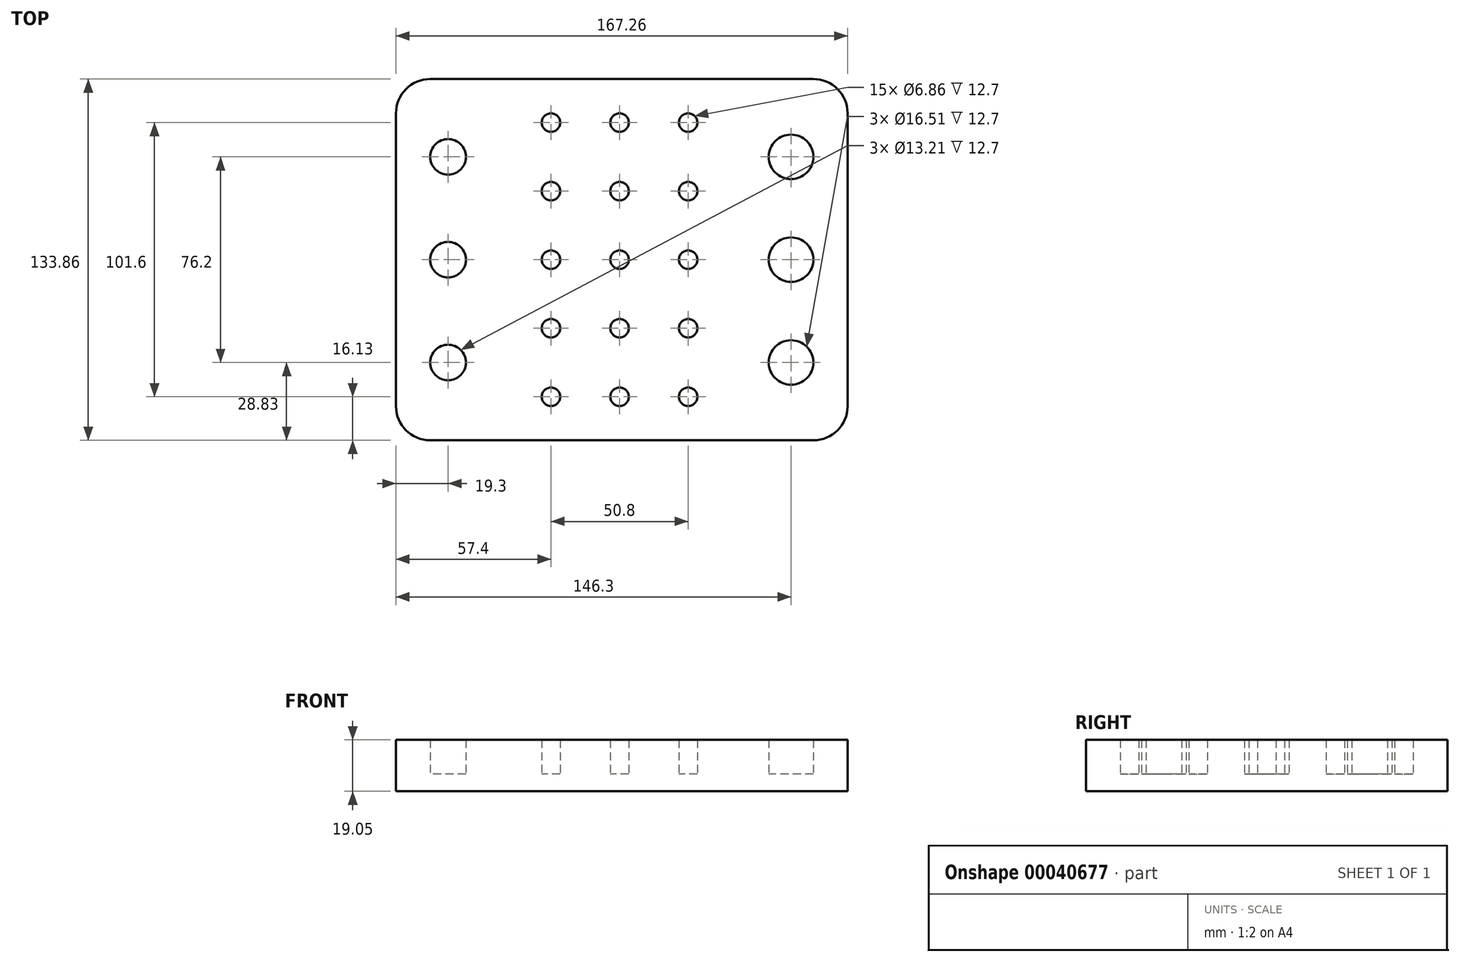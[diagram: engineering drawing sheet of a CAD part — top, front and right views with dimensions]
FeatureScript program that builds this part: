
annotation { "Feature Type Name" : "Feature", "Feature Type Description" : "" }
export const myFeature = defineFeature(function(context is Context, id is Id, definition is map)
    precondition{}
    {
        {
            var Q0;
            Q0=qCreatedBy(makeId("Top.planeOp"),FACE);
            var sketch = newSketch(context, id + "F0", { "sketchPlane" : qUnion([Q0])});
            skCircle(sketch, "E0", {"center": v(0, 0) * mm, "radius": 3.43 * mm});
            skCircle(sketch, "E1.0.1.0", {"center": v(0, 25.4) * mm, "radius": 3.43 * mm});
            skCircle(sketch, "E1.0.2.0", {"center": v(0, 50.8) * mm, "radius": 3.43 * mm});
            skCircle(sketch, "E1.1.0.0", {"center": v(25.4, 0) * mm, "radius": 3.43 * mm});
            skCircle(sketch, "E1.1.1.0", {"center": v(25.4, 25.4) * mm, "radius": 3.43 * mm});
            skCircle(sketch, "E1.1.2.0", {"center": v(25.4, 50.8) * mm, "radius": 3.43 * mm});
            skCircle(sketch, "E1.2.0.0", {"center": v(50.8, 0) * mm, "radius": 3.43 * mm});
            skCircle(sketch, "E1.2.1.0", {"center": v(50.8, 25.4) * mm, "radius": 3.43 * mm});
            skCircle(sketch, "E1.2.2.0", {"center": v(50.8, 50.8) * mm, "radius": 3.43 * mm});
            skLineSegment(sketch, "E1.direction1", {"start": v(0, 0) * mm, "end": v(25.4, 0) * mm, "construction": true});
            skLineSegment(sketch, "E1.direction2", {"start": v(0, 0) * mm, "end": v(0, 25.4) * mm, "construction": true});
            skCircle(sketch, "E2", {"center": v(88.9, 0) * mm, "radius": 8.26 * mm});
            skCircle(sketch, "E3", {"center": v(88.9, 38.1) * mm, "radius": 8.26 * mm});
            skCircle(sketch, "E4", {"center": v(-38.1, 0) * mm, "radius": 6.6 * mm});
            skCircle(sketch, "E5", {"center": v(-38.1, 38.1) * mm, "radius": 6.6 * mm});
            skCircle(sketch, "E6.MirrorC", {"center": v(0, -50.8) * mm, "radius": 3.43 * mm});
            skCircle(sketch, "E7.MirrorC", {"center": v(0, -25.4) * mm, "radius": 3.43 * mm});
            skCircle(sketch, "E8.MirrorC", {"center": v(25.4, -25.4) * mm, "radius": 3.43 * mm});
            skLineSegment(sketch, "E9.MirrorCS", {"start": v(0, 0) * mm, "end": v(25.4, 0) * mm});
            skLineSegment(sketch, "E10.MirrorCS", {"start": v(0, 0) * mm, "end": v(0, -25.4) * mm});
            skCircle(sketch, "E11.MirrorC", {"center": v(50.8, -50.8) * mm, "radius": 3.43 * mm});
            skCircle(sketch, "E12.MirrorC", {"center": v(25.4, -50.8) * mm, "radius": 3.43 * mm});
            skCircle(sketch, "E13.MirrorC", {"center": v(-38.1, -38.1) * mm, "radius": 6.6 * mm});
            skCircle(sketch, "E14.MirrorC", {"center": v(88.9, -38.1) * mm, "radius": 8.26 * mm});
            skCircle(sketch, "E15.MirrorC", {"center": v(50.8, -25.4) * mm, "radius": 3.43 * mm});
            skLineSegment(sketch, "E16.bottom", {"start": v(-57.4, -66.93) * mm, "end": v(109.86, -66.93) * mm});
            skLineSegment(sketch, "E16.top", {"start": v(-57.4, 66.93) * mm, "end": v(109.85, 66.93) * mm});
            skLineSegment(sketch, "E16.left", {"start": v(-57.4, -66.93) * mm, "end": v(-57.4, 66.93) * mm});
            skLineSegment(sketch, "E16.right", {"start": v(109.86, -66.93) * mm, "end": v(109.85, 66.93) * mm});
            skSolve(sketch);
        }
        {
            var Q0;
            Q0=makeQuery(id+"F0.imprint","IMPRINT",FACE,{"disambiguationData":[TD([[makeQuery(id+"F0.imprint","IMPRINT",EDGE,{"derivedFrom":sQuery(id+"F0.wireOp",EDGE,"E1.0.1.0")}),-1.0]])]});
            extrude(context, id + "F1", {"entities" : qUnion([Q0]), "depth" : 12.7 * mm});
        }
        {
            var Q0;
            Q0=makeQuery(id+"F1.opExtrude","CAP_FACE",FACE,{"disambiguationData":[OSD([sQuery(id+"F0.wireOp",EDGE,"E1.0.1.0"),sQuery(id+"F0.wireOp",EDGE,"E1.0.2.0"),sQuery(id+"F0.wireOp",EDGE,"E1.1.1.0"),sQuery(id+"F0.wireOp",EDGE,"E1.1.2.0"),sQuery(id+"F0.wireOp",EDGE,"E1.2.1.0"),sQuery(id+"F0.wireOp",EDGE,"E1.2.2.0"),sQuery(id+"F0.wireOp",EDGE,"E3"),sQuery(id+"F0.wireOp",EDGE,"E5"),sQuery(id+"F0.wireOp",EDGE,"E1.1.0.0"),sQuery(id+"F0.wireOp",EDGE,"E6.MirrorC"),sQuery(id+"F0.wireOp",EDGE,"E7.MirrorC"),sQuery(id+"F0.wireOp",EDGE,"E8.MirrorC"),sQuery(id+"F0.wireOp",EDGE,"E0"),sQuery(id+"F0.wireOp",EDGE,"E2"),sQuery(id+"F0.wireOp",EDGE,"E4"),sQuery(id+"F0.wireOp",EDGE,"E11.MirrorC"),sQuery(id+"F0.wireOp",EDGE,"E12.MirrorC"),sQuery(id+"F0.wireOp",EDGE,"E1.2.0.0"),sQuery(id+"F0.wireOp",EDGE,"E13.MirrorC"),sQuery(id+"F0.wireOp",EDGE,"E14.MirrorC"),sQuery(id+"F0.wireOp",EDGE,"E15.MirrorC"),sQuery(id+"F0.wireOp",EDGE,"E16.bottom"),sQuery(id+"F0.wireOp",EDGE,"E16.top"),sQuery(id+"F0.wireOp",EDGE,"E16.left"),sQuery(id+"F0.wireOp",EDGE,"E16.right")])],"isStart":true});
            var sketch = newSketch(context, id + "F2", { "sketchPlane" : qUnion([Q0])});
            skLineSegment(sketch, "E17.0", {"start": v(-57.4, 66.93) * mm, "end": v(109.86, 66.93) * mm});
            skLineSegment(sketch, "E18.0", {"start": v(-57.4, 66.93) * mm, "end": v(-57.4, -66.93) * mm});
            skLineSegment(sketch, "E19.0", {"start": v(-57.4, -66.93) * mm, "end": v(109.86, -66.93) * mm});
            skLineSegment(sketch, "E20.0", {"start": v(109.86, 66.93) * mm, "end": v(109.85, -66.93) * mm});
            skSolve(sketch);
        }
        {
            var Q0;
            Q0 = qSketchRegion(id + "F2", true);
            extrude(context, id + "F3", {"entities" : qUnion([Q0]), "operationType" : NewBodyOperationType.ADD, "depth" : 6.35 * mm});
        }
        {
            var Q0;
            Q0=makeQuery(id+"F3.boolean.opBoolean","MERGE",EDGE,{"derivedFrom":[makeQuery(id+"F1.opExtrude","SWEPT_EDGE",EDGE,{"disambiguationData":[OSD([sQuery(id+"F0.wireOp",EDGE,"E16.bottom"),sQuery(id+"F0.wireOp",EDGE,"E16.left")])]}),makeQuery(id+"F3.opExtrude","SWEPT_EDGE",EDGE,{"disambiguationData":[OSD([sQuery(id+"F2.wireOp",EDGE,"E17.0"),sQuery(id+"F2.wireOp",EDGE,"E18.0")])]})]});
            var Q1;
            Q1=makeQuery(id+"F3.boolean.opBoolean","MERGE",EDGE,{"derivedFrom":[makeQuery(id+"F1.opExtrude","SWEPT_EDGE",EDGE,{"disambiguationData":[OSD([sQuery(id+"F0.wireOp",EDGE,"E16.top"),sQuery(id+"F0.wireOp",EDGE,"E16.left")])]}),makeQuery(id+"F3.opExtrude","SWEPT_EDGE",EDGE,{"disambiguationData":[OSD([sQuery(id+"F2.wireOp",EDGE,"E18.0"),sQuery(id+"F2.wireOp",EDGE,"E19.0")])]})]});
            var Q2;
            Q2=makeQuery(id+"F3.boolean.opBoolean","MERGE",EDGE,{"derivedFrom":[makeQuery(id+"F1.opExtrude","SWEPT_EDGE",EDGE,{"disambiguationData":[OSD([sQuery(id+"F0.wireOp",EDGE,"E16.bottom"),sQuery(id+"F0.wireOp",EDGE,"E16.right")])]}),makeQuery(id+"F3.opExtrude","SWEPT_EDGE",EDGE,{"disambiguationData":[OSD([sQuery(id+"F2.wireOp",EDGE,"E17.0"),sQuery(id+"F2.wireOp",EDGE,"E20.0")])]})]});
            var Q3;
            Q3=makeQuery(id+"F3.boolean.opBoolean","MERGE",EDGE,{"derivedFrom":[makeQuery(id+"F1.opExtrude","SWEPT_EDGE",EDGE,{"disambiguationData":[OSD([sQuery(id+"F0.wireOp",EDGE,"E16.top"),sQuery(id+"F0.wireOp",EDGE,"E16.right")])]}),makeQuery(id+"F3.opExtrude","SWEPT_EDGE",EDGE,{"disambiguationData":[OSD([sQuery(id+"F2.wireOp",EDGE,"E19.0"),sQuery(id+"F2.wireOp",EDGE,"E20.0")])]})]});
            fillet(context, id + "F4", {"entities" : qUnion([Q0, Q1, Q2, Q3]), "radius" : 12.7 * mm, "tangentPropagation" : true, "allowEdgeOverflow" : false});
        }
    });
